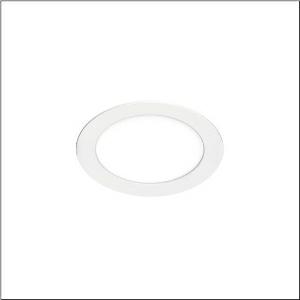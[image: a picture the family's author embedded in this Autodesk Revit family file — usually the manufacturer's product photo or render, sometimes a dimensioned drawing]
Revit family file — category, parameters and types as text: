
# Revit family: lunis_41_flat_51dr10mfgcb
name_source: partatom
category: Lighting Fixtures
units: mm (PartAtom-declared; Revit-internal decimal feet)

## family parameters
Cut with Voids When Loaded = No
Host = Face
Light Source = No
Part Type = Normal
Room Calculation Point = No
Round Connector Dimension = Use Diameter
Shared = No

## types (1)
- --- (1 x LED, 2430 lm, 19.5 W, 4000K)
    Apparent Load = 20 VA
    CIE Flux Codes = 49 80 96 100 100
    Color Rendering = 80
    Color Temperature = 4000K
    Default Elevation = 1800 mm
    Description = Lunis 41 Flat, downlight, light emission: direct distribution, LED rated luminous flux: 2.360lm, light colour: 830/840, mains connection: 230V, AC, 50/60Hz, housing, round, of aluminium, coated, traffic white (RAL 9016), diameter: 225mm, protection rating (complete): IP20, protection rating (on room side): IP44, insulation class (complete): insulation class II (safety insulation), certification: CE, permissible ambient temperature for indoor applications: -20..+40°C, packaging unit: 1 piece
    Height = 0 mm  [stored 0 ft]
    Lamp = 1 x LED
    Lamp Light Flux = 2430 lm
    Lamp Power = 19.5 W
    Lamp count = 1
    Length = 225 mm
    Luminous efficacy = 125 lm/W
    Manufacturer = Siteco
    ModVariant = No
    Model = 51DR10MFGCB
    Mounting Place = Ceiling
    Mounting Type = Recessed
    Number of Poles = 1
    OnlyDefault = Yes
    Power Factor = 1
    Product Name = Lunis 41 Flat
    Product group = downlight
    ProductGroupID = 401
    Protection Class = Protection class II
    Protection Degree = IP 20
    RLX_Detail_Level = 1
    RLX_Emergency_Light_Flux = 0 lm
    RLX_Emergency_Type = 0
    RLX_Emergency_Type_DB = No
    RlxData = <blob elided: 11573 chars, md5=b5117a02>
    Socket = socket
    Standby Power = 0 W
    System Light Flux = 2430 lm
    System Power = 20 W
    Type Comments = factory setting: colour temperature 4000K
    Type Image = l_1340923.jpg
    URL = http://relux.com
    VarID = @adj_020033
    Voltage = 0 V
    Weight = 0.00 kg
    Width = 0 mm  [stored 0 ft]

note: [stored X ft] marks values corroborated as IEEE doubles in the binary element streams (Revit-internal decimal feet)

## geometry (parser evidence)
native form markers: Sweep x10
no freeform markers — native parametric forms only
